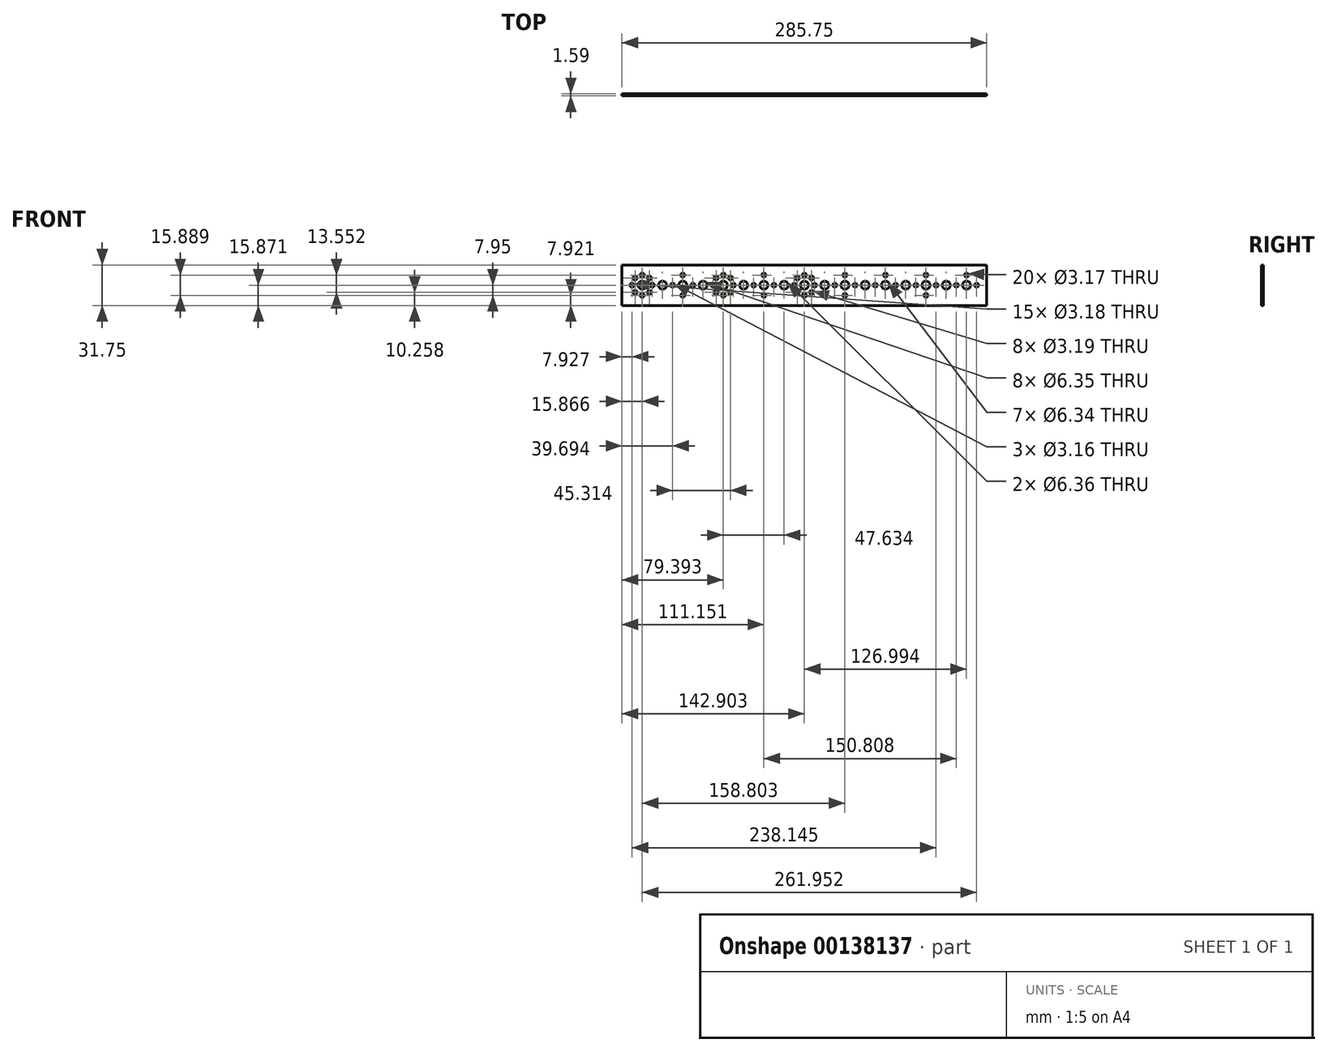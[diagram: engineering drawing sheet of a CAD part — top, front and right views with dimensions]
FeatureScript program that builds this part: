
annotation { "Feature Type Name" : "Feature", "Feature Type Description" : "" }
export const myFeature = defineFeature(function(context is Context, id is Id, definition is map)
    precondition{}
    {
        {
            var Q0;
            Q0=qCreatedBy(makeId("Front.planeOp"),FACE);
            var sketch = newSketch(context, id + "F0", { "sketchPlane" : qUnion([Q0])});
            skLineSegment(sketch, "E0.bottom", {"start": v(-72.37, -16.94) * mm, "end": v(213.38, -16.94) * mm});
            skLineSegment(sketch, "E0.top", {"start": v(-72.37, 14.8) * mm, "end": v(213.38, 14.8) * mm});
            skLineSegment(sketch, "E0.left", {"start": v(-72.37, -16.94) * mm, "end": v(-72.37, 14.8) * mm});
            skLineSegment(sketch, "E0.right", {"start": v(213.38, -16.94) * mm, "end": v(213.38, 14.8) * mm});
            skCircle(sketch, "E1", {"center": v(-64.44, -1.07) * mm, "radius": 1.6 * mm});
            skPoint(sketch, "E2.orphan", {"position": v(-66.03, -1.07) * mm});
            skPoint(sketch, "E3.start.orphan", {"position": v(-72.37, -1.07) * mm});
            skCircle(sketch, "E4", {"center": v(-48.56, -1.07) * mm, "radius": 1.6 * mm});
            skPoint(sketch, "E5.orphan", {"position": v(-50.16, -1.07) * mm});
            skPoint(sketch, "E6.start.orphan", {"position": v(-46.97, -1.07) * mm});
            skPoint(sketch, "E7.end.orphan", {"position": v(-62.85, -1.07) * mm});
            skPoint(sketch, "E8.trimOffspring.start.orphan", {"position": v(-59.67, -1.07) * mm});
            skLineSegment(sketch, "E9", {"start": v(-59.68, -1.07) * mm, "end": v(-59.67, -1.07) * mm});
            skCircle(sketch, "E10", {"center": v(-56.5, -1.07) * mm, "radius": 3.18 * mm});
            skPoint(sketch, "E11.orphan", {"position": v(-64.44, 12.68) * mm});
            skPoint(sketch, "E12.orphan", {"position": v(-64.44, -14.82) * mm});
            skCircle(sketch, "E13", {"center": v(-56.5, 6.87) * mm, "radius": 1.59 * mm});
            skPoint(sketch, "E14.orphan", {"position": v(-48.56, 6.87) * mm});
            skLineSegment(sketch, "E15.trimOffspring", {"start": v(-48.56, -1.07) * mm, "end": v(-48.56, -1.07) * mm});
            skCircle(sketch, "E16", {"center": v(-50.89, 4.54) * mm, "radius": 1.58 * mm});
            skPoint(sketch, "E17.orphan", {"position": v(-64.44, 6.87) * mm});
            skCircle(sketch, "E18", {"center": v(-62.12, 4.55) * mm, "radius": 1.59 * mm});
            skCircle(sketch, "E19", {"center": v(-62.12, -6.68) * mm, "radius": 1.59 * mm});
            skCircle(sketch, "E20", {"center": v(-50.89, -6.68) * mm, "radius": 1.6 * mm});
            skCircle(sketch, "E21", {"center": v(-56.5, -9.02) * mm, "radius": 1.59 * mm});
            skCircle(sketch, "E22", {"center": v(-40.61, -1.07) * mm, "radius": 3.18 * mm});
            skPoint(sketch, "E23.orphan", {"position": v(-37.44, -1.07) * mm});
            skPoint(sketch, "E24.end.orphan", {"position": v(-43.8, -1.07) * mm});
            skCircle(sketch, "E25", {"center": v(-32.68, -1.07) * mm, "radius": 1.58 * mm});
            skPoint(sketch, "E26.orphan", {"position": v(-34.26, -1.07) * mm});
            skCircle(sketch, "E27", {"center": v(-24.74, -1.07) * mm, "radius": 3.17 * mm});
            skCircle(sketch, "E28", {"center": v(-16.8, -1.07) * mm, "radius": 1.59 * mm});
            skPoint(sketch, "E29.start.orphan", {"position": v(-15.22, -1.07) * mm});
            skPoint(sketch, "E30.end.orphan", {"position": v(-18.4, -1.07) * mm});
            skPoint(sketch, "E31.orphan", {"position": v(-21.56, -1.07) * mm});
            skPoint(sketch, "E32.end.orphan", {"position": v(-27.91, -1.07) * mm});
            skPoint(sketch, "E32.start.orphan", {"position": v(-31.1, -1.07) * mm});
            skCircle(sketch, "E33", {"center": v(-24.74, 6.87) * mm, "radius": 1.59 * mm});
            skCircle(sketch, "E34", {"center": v(-24.74, -9.02) * mm, "radius": 1.59 * mm});
            skCircle(sketch, "E35", {"center": v(-0.92, -1.07) * mm, "radius": 1.59 * mm});
            skPoint(sketch, "E36.start.orphan", {"position": v(0.67, -1.07) * mm});
            skPoint(sketch, "E37.end.orphan", {"position": v(-2.51, -1.07) * mm});
            skCircle(sketch, "E38", {"center": v(-8.86, -1.07) * mm, "radius": 3.17 * mm});
            skPoint(sketch, "E39.orphan", {"position": v(-5.7, -1.07) * mm});
            skPoint(sketch, "E40.start.orphan", {"position": v(-12.04, -1.07) * mm});
            skCircle(sketch, "E41", {"center": v(7.02, -1.07) * mm, "radius": 3.18 * mm});
            skCircle(sketch, "E42", {"center": v(14.96, -1.07) * mm, "radius": 1.59 * mm});
            skCircle(sketch, "E43", {"center": v(22.9, -1.07) * mm, "radius": 3.17 * mm});
            skPoint(sketch, "E44.orphan", {"position": v(3.84, -1.07) * mm});
            skPoint(sketch, "E45.start.orphan", {"position": v(10.2, -1.07) * mm});
            skPoint(sketch, "E46.start.orphan", {"position": v(13.38, -1.07) * mm});
            skPoint(sketch, "E47.start.orphan", {"position": v(16.55, -1.07) * mm});
            skPoint(sketch, "E48.start.orphan", {"position": v(19.72, -1.07) * mm});
            skCircle(sketch, "E49", {"center": v(30.83, -1.07) * mm, "radius": 1.59 * mm});
            skCircle(sketch, "E50", {"center": v(38.78, -1.07) * mm, "radius": 3.17 * mm});
            skCircle(sketch, "E51", {"center": v(46.7, -1.07) * mm, "radius": 1.59 * mm});
            skCircle(sketch, "E52", {"center": v(54.66, -1.07) * mm, "radius": 3.18 * mm});
            skPoint(sketch, "E53.orphan", {"position": v(57.83, -1.07) * mm});
            skPoint(sketch, "E54.end.orphan", {"position": v(51.48, -1.07) * mm});
            skPoint(sketch, "E55.orphan", {"position": v(48.3, -1.07) * mm});
            skPoint(sketch, "E56.end.orphan", {"position": v(45.12, -1.07) * mm});
            skPoint(sketch, "E57.orphan", {"position": v(41.95, -1.07) * mm});
            skPoint(sketch, "E58.end.orphan", {"position": v(35.6, -1.07) * mm});
            skPoint(sketch, "E58.start.orphan", {"position": v(32.42, -1.07) * mm});
            skPoint(sketch, "E59.end.orphan", {"position": v(29.25, -1.07) * mm});
            skPoint(sketch, "E59.start.orphan", {"position": v(26.07, -1.07) * mm});
            skCircle(sketch, "E60", {"center": v(62.6, -1.07) * mm, "radius": 1.59 * mm});
            skPoint(sketch, "E61.orphan", {"position": v(61.02, -1.07) * mm});
            skPoint(sketch, "E62.start.orphan", {"position": v(64.2, -1.07) * mm});
            skCircle(sketch, "E63", {"center": v(70.53, -1.07) * mm, "radius": 3.17 * mm});
            skPoint(sketch, "E64.orphan", {"position": v(67.36, -1.07) * mm});
            skPoint(sketch, "E65.start.orphan", {"position": v(73.7, -1.07) * mm});
            skCircle(sketch, "E66", {"center": v(78.48, -1.07) * mm, "radius": 1.59 * mm});
            skPoint(sketch, "E67.orphan", {"position": v(76.89, -1.07) * mm});
            skPoint(sketch, "E68.start.orphan", {"position": v(80.06, -1.07) * mm});
            skCircle(sketch, "E69", {"center": v(86.41, -1.07) * mm, "radius": 3.17 * mm});
            skPoint(sketch, "E70.orphan", {"position": v(83.24, -1.07) * mm});
            skPoint(sketch, "E71.end.orphan", {"position": v(89.59, -1.07) * mm});
            skCircle(sketch, "E72", {"center": v(94.35, -1.07) * mm, "radius": 1.6 * mm});
            skCircle(sketch, "E73", {"center": v(102.3, -1.07) * mm, "radius": 3.17 * mm});
            skPoint(sketch, "E74.orphan", {"position": v(105.47, -1.07) * mm});
            skPoint(sketch, "E75.end.orphan", {"position": v(99.12, -1.07) * mm});
            skPoint(sketch, "E76.orphan", {"position": v(95.94, -1.07) * mm});
            skPoint(sketch, "E77.end.orphan", {"position": v(92.75, -1.07) * mm});
            skCircle(sketch, "E78", {"center": v(110.25, -1.07) * mm, "radius": 1.6 * mm});
            skCircle(sketch, "E79", {"center": v(118.18, -1.07) * mm, "radius": 3.17 * mm});
            skCircle(sketch, "E80", {"center": v(134.03, -1.07) * mm, "radius": 3.17 * mm});
            skCircle(sketch, "E81", {"center": v(126.1, -1.07) * mm, "radius": 1.58 * mm});
            skPoint(sketch, "E82.orphan", {"position": v(108.66, -1.07) * mm});
            skPoint(sketch, "E83.start.orphan", {"position": v(111.84, -1.07) * mm});
            skPoint(sketch, "E84.orphan", {"position": v(115.01, -1.07) * mm});
            skPoint(sketch, "E85.start.orphan", {"position": v(121.35, -1.07) * mm});
            skPoint(sketch, "E86.orphan", {"position": v(124.52, -1.07) * mm});
            skPoint(sketch, "E87.start.orphan", {"position": v(127.7, -1.07) * mm});
            skPoint(sketch, "E88.orphan", {"position": v(130.86, -1.07) * mm});
            skPoint(sketch, "E89.end.orphan", {"position": v(137.2, -1.07) * mm});
            skCircle(sketch, "E90", {"center": v(141.97, -1.07) * mm, "radius": 1.6 * mm});
            skCircle(sketch, "E91", {"center": v(149.92, -1.07) * mm, "radius": 3.17 * mm});
            skCircle(sketch, "E92", {"center": v(157.85, -1.07) * mm, "radius": 1.58 * mm});
            skPoint(sketch, "E93.orphan", {"position": v(159.43, -1.07) * mm});
            skPoint(sketch, "E94.end.orphan", {"position": v(156.26, -1.07) * mm});
            skPoint(sketch, "E95.orphan", {"position": v(153.09, -1.07) * mm});
            skPoint(sketch, "E96.orphan", {"position": v(140.38, -1.07) * mm});
            skPoint(sketch, "E97.end.orphan", {"position": v(146.75, -1.07) * mm});
            skPoint(sketch, "E97.start.orphan", {"position": v(143.57, -1.07) * mm});
            skCircle(sketch, "E98", {"center": v(165.76, -1.07) * mm, "radius": 3.17 * mm});
            skPoint(sketch, "E99.start.orphan", {"position": v(162.6, -1.07) * mm});
            skPoint(sketch, "E100.start.orphan", {"position": v(168.94, -1.07) * mm});
            skCircle(sketch, "E101", {"center": v(173.7, -1.07) * mm, "radius": 1.59 * mm});
            skPoint(sketch, "E102.orphan", {"position": v(172.11, -1.07) * mm});
            skCircle(sketch, "E103", {"center": v(181.64, -1.07) * mm, "radius": 3.17 * mm});
            skCircle(sketch, "E104", {"center": v(189.59, -1.07) * mm, "radius": 1.6 * mm});
            skPoint(sketch, "E105.end.orphan", {"position": v(191.18, -1.07) * mm});
            skPoint(sketch, "E106.end.orphan", {"position": v(188, -1.07) * mm});
            skPoint(sketch, "E107.start.orphan", {"position": v(175.3, -1.07) * mm});
            skPoint(sketch, "E108.orphan", {"position": v(178.47, -1.07) * mm});
            skPoint(sketch, "E109.end.orphan", {"position": v(184.81, -1.07) * mm});
            skCircle(sketch, "E110", {"center": v(197.53, -1.07) * mm, "radius": 3.17 * mm});
            skCircle(sketch, "E111", {"center": v(205.45, -1.07) * mm, "radius": 1.58 * mm});
            skPoint(sketch, "E112.orphan", {"position": v(207.03, -1.07) * mm});
            skPoint(sketch, "E113.end.orphan", {"position": v(203.87, -1.07) * mm});
            skPoint(sketch, "E114.orphan", {"position": v(200.7, -1.07) * mm});
            skPoint(sketch, "E115.end.orphan", {"position": v(194.36, -1.07) * mm});
            skCircle(sketch, "E116", {"center": v(7.02, 6.87) * mm, "radius": 1.59 * mm});
            skCircle(sketch, "E117", {"center": v(38.78, 6.87) * mm, "radius": 1.59 * mm});
            skCircle(sketch, "E118", {"center": v(70.53, 6.87) * mm, "radius": 1.59 * mm});
            skCircle(sketch, "E119", {"center": v(102.3, 6.87) * mm, "radius": 1.59 * mm});
            skCircle(sketch, "E120", {"center": v(134.03, 6.87) * mm, "radius": 1.6 * mm});
            skCircle(sketch, "E121", {"center": v(165.76, 6.87) * mm, "radius": 1.59 * mm});
            skCircle(sketch, "E122", {"center": v(197.53, 6.87) * mm, "radius": 1.58 * mm});
            skCircle(sketch, "E123", {"center": v(7.02, -9.02) * mm, "radius": 1.58 * mm});
            skCircle(sketch, "E124", {"center": v(1.4, 4.54) * mm, "radius": 1.58 * mm});
            skPoint(sketch, "E125.orphan", {"position": v(-0.92, 6.87) * mm});
            skCircle(sketch, "E126", {"center": v(1.4, -6.68) * mm, "radius": 1.59 * mm});
            skCircle(sketch, "E127", {"center": v(12.64, -6.68) * mm, "radius": 1.58 * mm});
            skCircle(sketch, "E128", {"center": v(12.64, 4.54) * mm, "radius": 1.58 * mm});
            skCircle(sketch, "E129", {"center": v(38.78, -9.02) * mm, "radius": 1.6 * mm});
            skLineSegment(sketch, "E130", {"start": v(38.78, -9.02) * mm, "end": v(40.37, -9.02) * mm});
            skCircle(sketch, "E131", {"center": v(70.53, -9.02) * mm, "radius": 1.59 * mm});
            skPoint(sketch, "E132.end.orphan", {"position": v(62.6, 6.87) * mm});
            skCircle(sketch, "E133", {"center": v(64.92, 4.55) * mm, "radius": 1.58 * mm});
            skCircle(sketch, "E134", {"center": v(64.92, -6.68) * mm, "radius": 1.59 * mm});
            skCircle(sketch, "E135", {"center": v(76.16, -6.68) * mm, "radius": 1.6 * mm});
            skCircle(sketch, "E136", {"center": v(76.16, 4.55) * mm, "radius": 1.59 * mm});
            skCircle(sketch, "E137", {"center": v(102.3, -9.02) * mm, "radius": 1.6 * mm});
            skCircle(sketch, "E138", {"center": v(165.76, -9.02) * mm, "radius": 1.6 * mm});
            skSolve(sketch);
        }
        {
            var Q0;
            Q0 = qSketchRegion(id + "F0", true);
            extrude(context, id + "F1", {"entities" : qUnion([Q0]), "depth" : 1.59 * mm});
        }
    });
